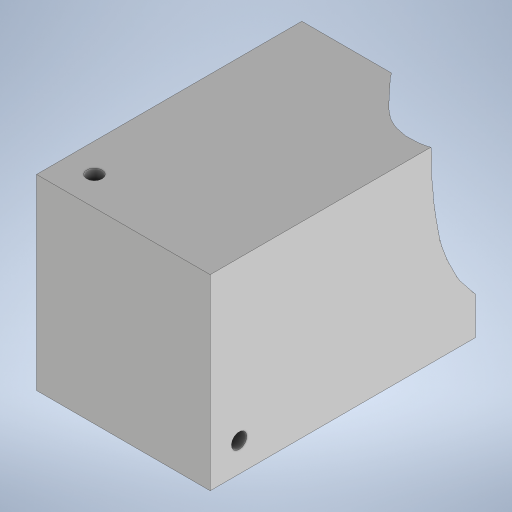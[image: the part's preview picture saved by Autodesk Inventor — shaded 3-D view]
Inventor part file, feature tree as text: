
AUTODESK INVENTOR PART (.ipt)
format: ipt  version: 2024 (Build 280153000, 153)  size: 10,651,136 bytes
history: native  units: mm
features: other x6, sketch x6, extrude x5, plane x2
ambient origin geometry x8: Origin, YZ Plane, XZ Plane, XY Plane, X Axis, Y Axis, Z Axis, Center Point
bodies: Body1 (feature_tree)
feature tree (19):
  other  "M.ipt"
  plane  "Plano de trabajo1"
  extrude  "Extrusión1"  [1 undecoded]
  other  "Combinar1"
  sketch  "Boceto3"  dims[d2=550.0mm d3=520.0mm]
  sketch  "Boceto4"  dims[d4=550.0mm d5=0.0mm d6=129.8482mm]
  plane  "Plano de trabajo2"
  sketch  "Boceto5"  dims[d17=180.0mm d18=180.0mm]
  extrude  "Extrusión2"  Depth=520.0mm
  extrude  "Extrusión3"  Depth=129.8482mm
  extrude  "Extrusión4"  Depth=180.0mm
  extrude  "Extrusión5"  Depth=180.0mm
  other  "Sólido1::M.ipt"
  other  "OperaciónIdentificador1"
  sketch  "Boceto1"  dims[d0=25.0mm d1=-365.0mm]
  other  "Sólido2"
  sketch  "Boceto6"  dims[d22=326.0mm d23=180.0mm]
  sketch  "Boceto7"  dims[d24=180.0mm d25=180.0mm d26=10.0mm d27=0.0mm d28=10.0mm d29=0.0mm d30=30.0mm d31=30.0mm d32=16.0mm d33=16.0mm d34=0.0mm d35=30.0mm d36=30.0mm d37=16.0mm d38=16.0mm d39=0.0mm d14=0.5mm d15=0.872665mm d16=0.5mm d19=0.5mm d20=0.872665mm d21=0.5mm]
  other  "Sólido1"
note: 1 required parameter value undecoded (feature->parameter linkage not recoverable at this tier; creation-order binding heuristic only, values carry confidence <= 0.55)
